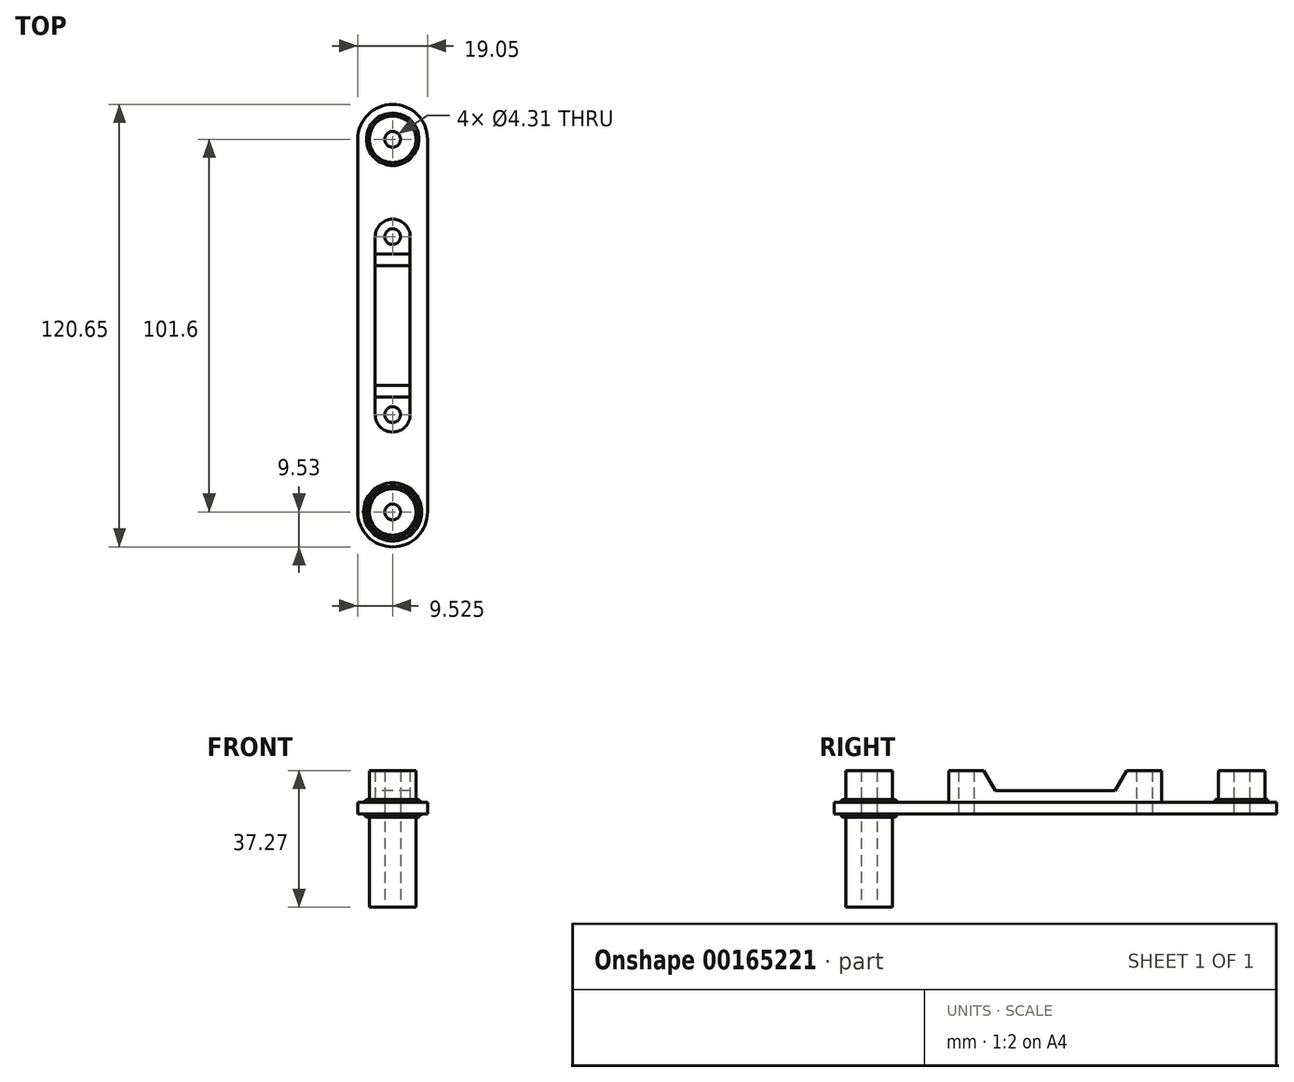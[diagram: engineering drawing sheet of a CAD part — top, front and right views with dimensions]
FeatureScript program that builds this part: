
annotation { "Feature Type Name" : "Feature", "Feature Type Description" : "" }
export const myFeature = defineFeature(function(context is Context, id is Id, definition is map)
    precondition{}
    {
        {
            var Q0;
            Q0=qCreatedBy(makeId("Top.planeOp"),FACE);
            var sketch = newSketch(context, id + "F0", { "sketchPlane" : qUnion([Q0])});
            skLineSegment(sketch, "E0.bottom", {"start": v(0, 0) * mm, "end": v(19.05, 0) * mm, "construction": true});
            skLineSegment(sketch, "E0.top", {"start": v(0, 101.6) * mm, "end": v(19.05, 101.6) * mm, "construction": true});
            skLineSegment(sketch, "E0.left", {"start": v(0, 0) * mm, "end": v(0, 101.6) * mm});
            skLineSegment(sketch, "E0.right", {"start": v(19.05, 0) * mm, "end": v(19.05, 101.6) * mm});
            skArc(sketch, "E1", {"start": v(19.05, 101.6) * mm, "mid": v(9.52, 111.13) * mm, "end": v(0, 101.6) * mm});
            skArc(sketch, "E2", {"start": v(0, 0) * mm, "mid": v(9.53, -9.52) * mm, "end": v(19.05, 0) * mm});
            skSolve(sketch);
        }
        {
            var Q0;
            Q0 = qSketchRegion(id + "F0", true);
            extrude(context, id + "F1", {"entities" : qUnion([Q0]), "depth" : 3.17 * mm});
        }
        {
            var Q0;
            Q0=makeQuery(id+"F1.opExtrude","CAP_FACE",FACE,{"disambiguationData":[OSD([sQuery(id+"F0.wireOp",EDGE,"E0.left"),sQuery(id+"F0.wireOp",EDGE,"E0.right"),sQuery(id+"F0.wireOp",EDGE,"E1"),sQuery(id+"F0.wireOp",EDGE,"E2")])],"isStart":false});
            var sketch = newSketch(context, id + "F2", { "sketchPlane" : qUnion([Q0])});
            skLineSegment(sketch, "E3", {"start": v(0, 50.8) * mm, "end": v(19.05, 50.8) * mm, "construction": true});
            skLineSegment(sketch, "E4.bottom", {"start": v(14.29, 79.83) * mm, "end": v(4.76, 79.83) * mm});
            skLineSegment(sketch, "E4.top", {"start": v(14.29, 21.77) * mm, "end": v(4.76, 21.77) * mm});
            skLineSegment(sketch, "E4.left", {"start": v(14.29, 79.83) * mm, "end": v(14.29, 21.77) * mm});
            skLineSegment(sketch, "E4.right", {"start": v(4.76, 79.83) * mm, "end": v(4.76, 21.77) * mm});
            skPoint(sketch, "E4.middle", {"position": v(9.52, 50.8) * mm});
            skCircle(sketch, "E5", {"center": v(9.52, 0) * mm, "radius": 6.35 * mm});
            skCircle(sketch, "E6", {"center": v(9.52, 101.6) * mm, "radius": 6.35 * mm});
            skSolve(sketch);
        }
        {
            var Q0;
            Q0 = qSketchRegion(id + "F2", true);
            extrude(context, id + "F3", {"entities" : qUnion([Q0]), "operationType" : NewBodyOperationType.ADD, "depth" : 8.7 * mm});
        }
        {
            var Q0;
            Q0=makeQuery(id+"F3.opExtrude","SWEPT_FACE",FACE,{"disambiguationData":[OSD([sQuery(id+"F2.wireOp",EDGE,"E4.right")])]});
            var sketch = newSketch(context, id + "F4", { "sketchPlane" : qUnion([Q0])});
            skLineSegment(sketch, "E7.bottom", {"start": v(-31.3, 11.87) * mm, "end": v(-70.3, 11.87) * mm});
            skLineSegment(sketch, "E7.top", {"start": v(-34.49, 6.35) * mm, "end": v(-67.11, 6.35) * mm});
            skLineSegment(sketch, "E7.right", {"start": v(-70.3, 11.87) * mm, "end": v(-67.11, 6.35) * mm});
            skLineSegment(sketch, "E8", {"start": v(-50.8, 6.35) * mm, "end": v(-50.8, 3.18) * mm, "construction": true});
            skLineSegment(sketch, "E9", {"start": v(-70.3, 11.87) * mm, "end": v(-70.3, 7.52) * mm, "construction": true});
            skLineSegment(sketch, "E10", {"start": v(-70.3, 7.52) * mm, "end": v(-79.83, 7.52) * mm, "construction": true});
            skLineSegment(sketch, "E11", {"start": v(-34.49, 6.35) * mm, "end": v(-31.3, 11.87) * mm});
            skPoint(sketch, "E12", {"position": v(-50.8, 11.87) * mm});
            skSolve(sketch);
        }
        {
            var Q0;
            Q0 = qSketchRegion(id + "F4", true);
            var Q1;
            Q1=makeQuery(id+"F3.opExtrude","SWEPT_FACE",FACE,{"disambiguationData":[OSD([sQuery(id+"F2.wireOp",EDGE,"E4.left")])]});
            extrude(context, id + "F5", {"entities" : qUnion([Q0]), "operationType" : NewBodyOperationType.REMOVE, "endBound" : BoundingType.UP_TO_SURFACE, "oppositeDirection" : true, "endBoundEntityFace" : qUnion([Q1]), "depth" : 25.4 * mm});
        }
        {
            var Q0;
            Q0=makeQuery(id+"F3.opExtrude","SWEPT_EDGE",EDGE,{"disambiguationData":[OSD([sQuery(id+"F2.wireOp",EDGE,"E4.bottom"),sQuery(id+"F2.wireOp",EDGE,"E4.right")])]});
            var Q1;
            Q1=makeQuery(id+"F3.opExtrude","SWEPT_EDGE",EDGE,{"disambiguationData":[OSD([sQuery(id+"F2.wireOp",EDGE,"E4.bottom"),sQuery(id+"F2.wireOp",EDGE,"E4.left")])]});
            var Q2;
            Q2=makeQuery(id+"F3.opExtrude","SWEPT_EDGE",EDGE,{"disambiguationData":[OSD([sQuery(id+"F2.wireOp",EDGE,"E4.top"),sQuery(id+"F2.wireOp",EDGE,"E4.right")])]});
            var Q3;
            Q3=makeQuery(id+"F3.opExtrude","SWEPT_EDGE",EDGE,{"disambiguationData":[OSD([sQuery(id+"F2.wireOp",EDGE,"E4.top"),sQuery(id+"F2.wireOp",EDGE,"E4.left")])]});
            fillet(context, id + "F6", {"entities" : qUnion([Q0, Q1, Q2, Q3]), "radius" : 4.76 * mm, "tangentPropagation" : true, "allowEdgeOverflow" : false});
        }
        {
            var Q0;
            Q0=makeQuery(id+"F1.opExtrude","CAP_FACE",FACE,{"disambiguationData":[OSD([sQuery(id+"F0.wireOp",EDGE,"E0.left"),sQuery(id+"F0.wireOp",EDGE,"E0.right"),sQuery(id+"F0.wireOp",EDGE,"E1"),sQuery(id+"F0.wireOp",EDGE,"E2")])],"isStart":true});
            var sketch = newSketch(context, id + "F7", { "sketchPlane" : qUnion([Q0])});
            skCircle(sketch, "E13", {"center": v(9.52, 0) * mm, "radius": 6.35 * mm});
            skSolve(sketch);
        }
        {
            var Q0;
            Q0 = qSketchRegion(id + "F7", true);
            extrude(context, id + "F8", {"entities" : qUnion([Q0]), "operationType" : NewBodyOperationType.ADD, "depth" : 25.4 * mm});
        }
        {
            var Q0;
            Q0=makeQuery(id+"F8.opExtrude","CAP_FACE",FACE,{"disambiguationData":[OSD([sQuery(id+"F7.wireOp",EDGE,"E13")])],"isStart":false});
            var sketch = newSketch(context, id + "F9", { "sketchPlane" : qUnion([Q0])});
            skCircle(sketch, "E14", {"center": v(9.52, 0) * mm, "radius": 2.15 * mm});
            skCircle(sketch, "E15", {"center": v(9.52, -26.54) * mm, "radius": 2.15 * mm});
            skCircle(sketch, "E16", {"center": v(9.52, -75.06) * mm, "radius": 2.15 * mm});
            skCircle(sketch, "E17", {"center": v(9.52, -101.6) * mm, "radius": 2.15 * mm});
            skSolve(sketch);
        }
        {
            var Q0;
            Q0 = qSketchRegion(id + "F9", true);
            var Q1;
            Q1=makeQuery(id+"F3.opExtrude","CAP_FACE",FACE,{"disambiguationData":[OSD([sQuery(id+"F2.wireOp",EDGE,"E5")])],"isStart":false});
            extrude(context, id + "F10", {"entities" : qUnion([Q0]), "operationType" : NewBodyOperationType.REMOVE, "endBound" : BoundingType.UP_TO_SURFACE, "oppositeDirection" : true, "endBoundEntityFace" : qUnion([Q1]), "depth" : 25.4 * mm});
        }
        {
            var Q0;
            Q0=makeQuery(id+"F1.opExtrude","CAP_FACE",FACE,{"disambiguationData":[OSD([sQuery(id+"F0.wireOp",EDGE,"E0.left"),sQuery(id+"F0.wireOp",EDGE,"E0.right"),sQuery(id+"F0.wireOp",EDGE,"E1"),sQuery(id+"F0.wireOp",EDGE,"E2")])],"isStart":false});
            var sketch = newSketch(context, id + "F11", { "sketchPlane" : qUnion([Q0])});
            skCircle(sketch, "E18", {"center": v(9.52, 0) * mm, "radius": 7.14 * mm});
            skCircle(sketch, "E19", {"center": v(9.52, 0) * mm, "radius": 2.15 * mm});
            skSolve(sketch);
        }
        {
            var Q0;
            Q0 = qSketchRegion(id + "F11", true);
            extrude(context, id + "F12", {"entities" : qUnion([Q0]), "operationType" : NewBodyOperationType.ADD, "depth" : 0.8 * mm, "hasSecondDirection" : true, "secondDirectionOppositeDirection" : true, "secondDirectionDepth" : 3.97 * mm});
        }
        {
            var Q0;
            Q0=makeQuery(id+"F1.opExtrude","CAP_FACE",FACE,{"disambiguationData":[OSD([sQuery(id+"F0.wireOp",EDGE,"E0.left"),sQuery(id+"F0.wireOp",EDGE,"E0.right"),sQuery(id+"F0.wireOp",EDGE,"E1"),sQuery(id+"F0.wireOp",EDGE,"E2")])],"isStart":false});
            var sketch = newSketch(context, id + "F13", { "sketchPlane" : qUnion([Q0])});
            skCircle(sketch, "E20", {"center": v(9.52, 101.6) * mm, "radius": 2.15 * mm});
            skCircle(sketch, "E21", {"center": v(9.52, 101.6) * mm, "radius": 7.14 * mm});
            skSolve(sketch);
        }
        {
            var Q0;
            Q0 = qSketchRegion(id + "F13", true);
            var Q1;
            Q1=makeQuery(id+"F12.opExtrude","CAP_FACE",FACE,{"disambiguationData":[OSD([sQuery(id+"F11.wireOp",EDGE,"E18"),sQuery(id+"F11.wireOp",EDGE,"E19")])],"isStart":false});
            extrude(context, id + "F14", {"entities" : qUnion([Q0]), "operationType" : NewBodyOperationType.ADD, "endBound" : BoundingType.UP_TO_SURFACE, "endBoundEntityFace" : qUnion([Q1]), "depth" : 25.4 * mm});
        }
        {
            var Q0;
            Q0=makeQuery(id+"F14.opExtrude","CAP_EDGE",EDGE,{"disambiguationData":[OSD([sQuery(id+"F13.wireOp",EDGE,"E21")])],"isStart":true});
            var Q1;
            Q1=makeQuery(id+"F12.boolean.opBoolean","INTERSECT",EDGE,{"derivedFrom":[makeQuery(id+"F1.opExtrude","CAP_FACE",FACE,{"disambiguationData":[OSD([sQuery(id+"F0.wireOp",EDGE,"E0.left"),sQuery(id+"F0.wireOp",EDGE,"E0.right"),sQuery(id+"F0.wireOp",EDGE,"E1"),sQuery(id+"F0.wireOp",EDGE,"E2")])],"isStart":true}),makeQuery(id+"F12.opExtrude","SWEPT_FACE",FACE,{"disambiguationData":[OSD([sQuery(id+"F11.wireOp",EDGE,"E18")])]})]});
            var Q2;
            Q2=makeQuery(id+"F12.boolean.opBoolean","INTERSECT",EDGE,{"derivedFrom":[makeQuery(id+"F1.opExtrude","CAP_FACE",FACE,{"disambiguationData":[OSD([sQuery(id+"F0.wireOp",EDGE,"E0.left"),sQuery(id+"F0.wireOp",EDGE,"E0.right"),sQuery(id+"F0.wireOp",EDGE,"E1"),sQuery(id+"F0.wireOp",EDGE,"E2")])],"isStart":false}),makeQuery(id+"F12.opExtrude","SWEPT_FACE",FACE,{"disambiguationData":[OSD([sQuery(id+"F11.wireOp",EDGE,"E18")])]})]});
            chamfer(context, id + "F15", {"entities" : qUnion([Q0, Q1, Q2]), "width" : 0.8 * mm, "tangentPropagation" : true});
        }
    });
